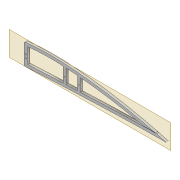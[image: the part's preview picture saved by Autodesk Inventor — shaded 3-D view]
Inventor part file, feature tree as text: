
AUTODESK INVENTOR PART (.ipt)
format: ipt  version: 2022 (Build 260153000, 153)  size: 346,112 bytes
history: native  units: mm
features: extrude x6, sketch x5, projected_geometry x4, shell x1, fillet x1, plane x1
ambient origin geometry x8: Origin, YZ Plane, XZ Plane, XY Plane, X Axis, Y Axis, Z Axis, Center Point
bodies: Solid1 (feature_tree)
feature tree (18):
  extrude  "Extrusion1"  Depth=5.0mm
  shell  "Shell1"  Thickness=6.0mm
  extrude  "Extrusion2"  Depth=2.0mm
  extrude  "Extrusion3"  Depth=5.9mm
  extrude  "Extrusion4"  Depth=10.0mm TaperAngle=0.0deg
  fillet  "Fillet1"  Radius=65.0mm
  extrude  "Extrusion5"  Depth=0.5mm TaperAngle=0.0deg
  plane  "Work Plane2"
  extrude  "Extrusion8"  Depth=0.5mm
  sketch  "Sketch3"  dims[d0=4.0mm d1=0.0mm d2=5.0mm d3=6.0mm]
  projected_geometry  "Projected Loop3"
  sketch  "Sketch8"  dims[d5=4.0mm d6=0.0mm d7=2.0mm]
  sketch  "Sketch9"  dims[d8=2.0mm d9=5.9mm]
  sketch  "Sketch10"  dims[d12=8.0mm d13=10.0mm d14=0.0mm d15=65.0mm]
  projected_geometry  "Projected Loop4"
  projected_geometry  "Projected Loop10"
  sketch  "Sketch16"  dims[d16=10.0mm d17=0.0mm d22=4.0mm d23=0.0mm d24=2.0mm d26=2.0mm d31=2.0mm d32=5.0mm d34=1.6mm d35=2.5mm d37=5.0mm d38=1.6mm d40=2.5mm d41=65.0mm d42=20.0mm d43=0.5mm d44=10.0mm d45=0.0mm]
  projected_geometry  "Projected Loop11"
